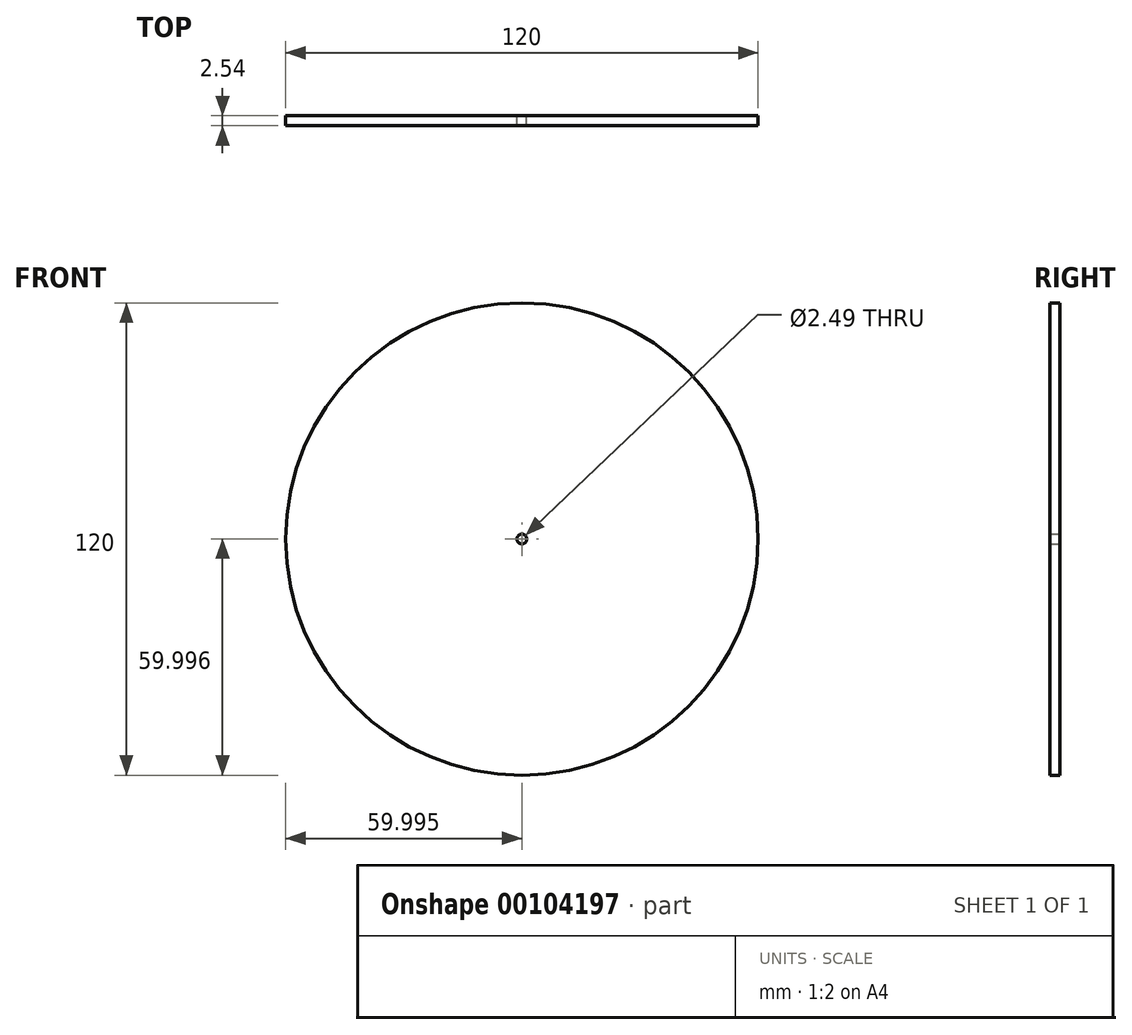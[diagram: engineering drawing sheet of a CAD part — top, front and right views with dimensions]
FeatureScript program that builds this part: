
annotation { "Feature Type Name" : "Feature", "Feature Type Description" : "" }
export const myFeature = defineFeature(function(context is Context, id is Id, definition is map)
    precondition{}
    {
        {
            var Q0;
            Q0=qCreatedBy(makeId("Front.planeOp"),FACE);
            var sketch = newSketch(context, id + "F0", { "sketchPlane" : qUnion([Q0])});
            skCircle(sketch, "E0", {"center": v(-35.08, 28.1) * mm, "radius": 60 * mm});
            skCircle(sketch, "E1", {"center": v(-35.08, 28.1) * mm, "radius": 1.24 * mm});
            skSolve(sketch);
        }
        {
            var Q0;
            Q0=makeQuery(id+"F0.imprint","IMPRINT",FACE,{"disambiguationData":[TD([[makeQuery(id+"F0.imprint","IMPRINT",EDGE,{"derivedFrom":sQuery(id+"F0.wireOp",EDGE,"E0")}),1.0]])]});
            extrude(context, id + "F1", {"entities" : qUnion([Q0]), "depth" : 2.54 * mm});
        }
    });
